# Revit family: RN 18054 Filtro fine con flange risciacquabile
name_source: partatom
category: Rohrzubehör
units: mm (PartAtom-declared; Revit-internal decimal feet)

## family parameters
Arbeitsebenenbasiert = Nein
Beim Laden mit Abzugskörper schneiden = Nein
Bemaßung runder Anschluss = Durchmesser verwenden
Gemeinsam genutzt = Nein
Immer vertikal = Ja
Teiletyp = Ventil - Zerlegung in

## types (3) — shared parameters
1.010.00.2 Blattnummer der Richtlinie = 17
1.010.00.3 Ausgabedatum (Monat) der Richtlinie = 201601
1.010.00.4 Herstellername = R. Nussbaum AG
1.010.00.5 Revisionsdatum der Datei = 20190528
1.010.00.6 Webadresse des Herstellers = http://www.nussbaum.ch
1.100.00.3 Sortiernummer für Anzeigereihenfolge = 9
1.100.00.4 Produktbezeichnung = Filterkombination, Filter und Schmutzfänger
1.960/3L.00.8 Link (URL) = https://www.nussbaum.ch
17.700.00.4 Armaturentyp = 1
17.700.00.7 Maximale Betriebstemperatur TB [°C] = 30
17.700.00.8 Maximaler Betriebsdruck (Arbeitsdruck) ps [1.0 · 105 Pa] = 16
CONNECTOR2_DIAMETER_dZ_0r = 8 mm  [stored 0.0262467 ft]
CONNECTOR2_dZ_00 = 75 mm
CONNECTOR2_dZ_01 = 76 mm
CONNECTOR2_ref_dX = 78 mm
CONNECTOR2_ref_dZ = 76 mm
CONNECTOR3_DIAMETER_dZ_0r = 8 mm  [stored 0.0262467 ft]
CONNECTOR3_dZ_00 = 75 mm
CONNECTOR3_dZ_01 = 76 mm
CONNECTOR3_ref_dX = 32 mm
CONNECTOR3_ref_dZ = 76 mm
CONNECTOR4_DIAMETER_dZ_0r = 8 mm  [stored 0.0262467 ft]
CONNECTOR4_dZ_00 = 75 mm
CONNECTOR4_dZ_01 = 76 mm
CONNECTOR4_ref_dX = 58 mm
CONNECTOR4_ref_dZ = 76 mm
Connector Visibility = Nein
EnclosingSpace Visibility = Nein
Hersteller = R. Nussbauzm AG
URL = https://www.nussbaum.ch

## per-type parameters (varying)
| type | 1.800.00.3 TGA-Nummer | 1.810.00.3 Hersteller-Bestellnummer | 1.810.00.4 DATANORM-Nummer | 1.810.00.5 StLB-Nummer | 1.810.00.6 GTIN-Nummer | 17.700.00.30 Produktbeschreibung | 17.700.00.5 Nennweite DN | 17.700.00.6 kvs-Wert [m3/h] | CONNECTOR0_DIAMETER_dX_0r | CONNECTOR0_dX_00 | CONNECTOR0_dX_01 | CONNECTOR0_ref_dX | CONNECTOR1_DIAMETER_dX_0r | CONNECTOR1_dX_00 | CONNECTOR1_dX_01 | CONNECTOR1_ref_dX | Modell | R. Nussbaum AG 18054.23 de Visibility | R. Nussbaum AG 18054.24 de Visibility | R. Nussbaum AG 18054.25 de Visibility | Typenkommentare |
| DN 65 | 00901400000000000000000000000200700000000000000001???00000 | 18054.23 | 18054.23 | 717.417 | 7612945819161 | 18054.23, Feinfilter mit Flanschen rückspülbar, Filterfeinheit 240 Mikron, DN=65 | 65 | 69.63 | 65 mm | 169 mm | 168 mm | 169 mm | 65 mm | 122 mm | 123 mm | 123 mm | 18054.23 | Ja | Nein | Nein | Filtro fine con flange risciacquabileDN 65 |
| DN 80 | 00901400000000000000000000000200700000000000000002???00000 | 18054.24 | 18054.24 | 717.418 | 7612945819178 | 18054.24, Feinfilter mit Flanschen rückspülbar, Filterfeinheit 240 Mikron, DN=80 | 80 | 74.26 | 80 mm | 179 mm | 178 mm | 179 mm | 80 mm | 132 mm | 133 mm | 133 mm | 18054.24 | Nein | Ja | Nein | Filtro fine con flange risciacquabileDN 80 |
| DN 100 | 00901400000000000000000000000200700000000000000003???00000 | 18054.25 | 18054.25 | 717.421 | 7612945819185 | 18054.25, Feinfilter mit Flanschen rückspülbar, Filterfeinheit 240 Mikron, DN=100 | 100 | 74 | 100 mm  [stored 0.328084 ft] | 199 mm | 198 mm | 199 mm | 100 mm  [stored 0.328084 ft] | 152 mm | 153 mm | 153 mm | 18054.25 | Nein | Nein | Ja | Filtro fine con flange risciacquabileDN 100 |

note: [stored X ft] marks values corroborated as IEEE doubles in the binary element streams (Revit-internal decimal feet)

## geometry (parser evidence)
native form markers: Sweep x1
no freeform markers — native parametric forms only
